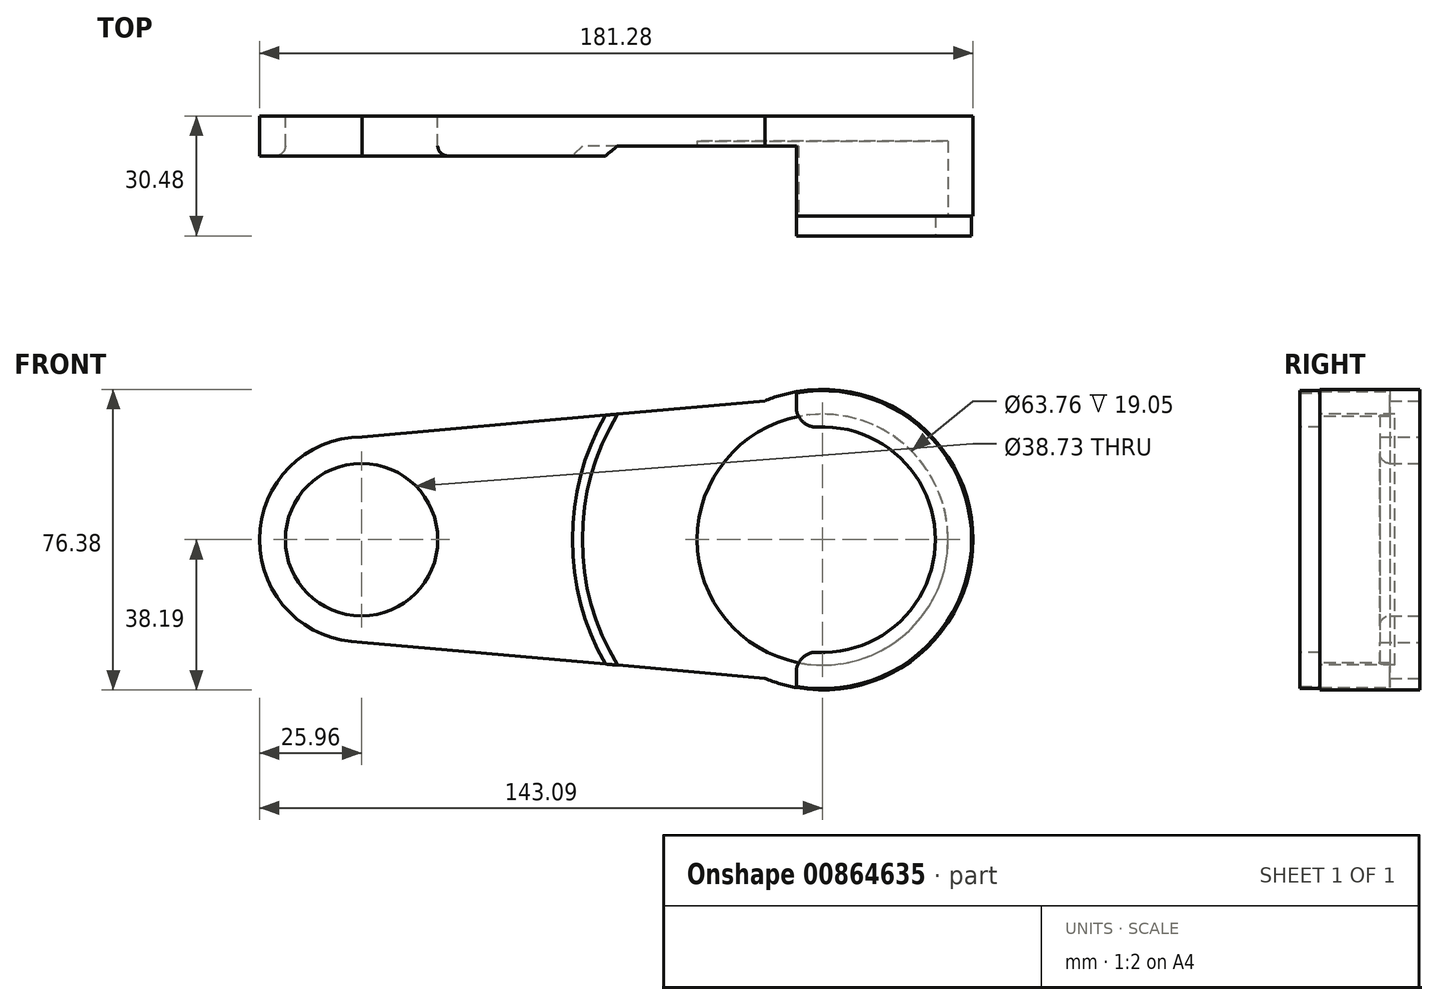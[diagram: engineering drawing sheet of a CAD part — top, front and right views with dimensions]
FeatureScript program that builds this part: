
annotation { "Feature Type Name" : "Feature", "Feature Type Description" : "" }
export const myFeature = defineFeature(function(context is Context, id is Id, definition is map)
    precondition{}
    {
        {
            var Q0;
            Q0=qCreatedBy(makeId("Front.planeOp"),FACE);
            var sketch = newSketch(context, id + "F0", { "sketchPlane" : qUnion([Q0])});
            skCircle(sketch, "E0", {"center": v(0, 0) * mm, "radius": 38.2 * mm});
            skSolve(sketch);
        }
        {
            var Q0;
            Q0 = qSketchRegion(id + "F0", true);
            extrude(context, id + "F1", {"entities" : qUnion([Q0]), "depth" : 25.4 * mm, "offsetDistance" : 25.4 * mm});
        }
        {
            var Q0;
            Q0=makeQuery(id+"F1.opExtrude","CAP_FACE",FACE,{"disambiguationData":[OSD([sQuery(id+"F0.wireOp",EDGE,"E0")])],"isStart":false});
            var sketch = newSketch(context, id + "F2", { "sketchPlane" : qUnion([Q0])});
            skCircle(sketch, "E1", {"center": v(0, 0) * mm, "radius": 31.88 * mm});
            skSolve(sketch);
        }
        {
            var Q0;
            Q0=makeQuery(id+"F2.imprint","IMPRINT",FACE,{"disambiguationData":[TD([[makeQuery(id+"F2.imprint","IMPRINT",EDGE,{"derivedFrom":sQuery(id+"F2.wireOp",EDGE,"E1")}),1.0]])]});
            extrude(context, id + "F3", {"entities" : qUnion([Q0]), "operationType" : NewBodyOperationType.REMOVE, "oppositeDirection" : true, "depth" : 19.05 * mm, "offsetDistance" : 25.4 * mm});
        }
        {
            var Q0;
            Q0=makeQuery(id+"F1.opExtrude","CAP_FACE",FACE,{"disambiguationData":[OSD([sQuery(id+"F0.wireOp",EDGE,"E0")])],"isStart":false});
            var sketch = newSketch(context, id + "F4", { "sketchPlane" : qUnion([Q0])});
            skSolve(sketch);
        }
        {
            var Q0;
            Q0=makeQuery(id+"F4.imprint","IMPRINT",FACE,{"disambiguationData":[TD([[makeQuery(id+"F4.imprint","IMPRINT",EDGE,{"derivedFrom":makeQuery(id+"F1.opExtrude","CAP_EDGE",EDGE,{"disambiguationData":[OSD([sQuery(id+"F0.wireOp",EDGE,"E0")])],"isStart":false})}),1.0]])]});
            var sketch = newSketch(context, id + "F5", { "sketchPlane" : qUnion([Q0])});
            skCircle(sketch, "E2", {"center": v(0, 0) * mm, "radius": 37.85 * mm});
            skSolve(sketch);
        }
        {
            var Q0;
            Q0 = qSketchRegion(id + "F5", true);
            extrude(context, id + "F6", {"entities" : qUnion([Q0]), "operationType" : NewBodyOperationType.ADD, "depth" : 5.08 * mm, "offsetDistance" : 25.4 * mm});
        }
        {
            var Q0;
            Q0=makeQuery(id+"F6.opExtrude","CAP_FACE",FACE,{"disambiguationData":[OSD([sQuery(id+"F5.wireOp",EDGE,"E2")])],"isStart":false});
            var sketch = newSketch(context, id + "F7", { "sketchPlane" : qUnion([Q0])});
            skCircle(sketch, "E3", {"center": v(0, 0) * mm, "radius": 28.64 * mm});
            skSolve(sketch);
        }
        {
            var Q0;
            Q0 = qSketchRegion(id + "F7", true);
            extrude(context, id + "F8", {"entities" : qUnion([Q0]), "operationType" : NewBodyOperationType.REMOVE, "oppositeDirection" : true, "depth" : 12.7 * mm, "offsetDistance" : 25.4 * mm});
        }
        {
            var Q0;
            Q0=makeQuery(id+"F6.opExtrude","CAP_FACE",FACE,{"disambiguationData":[OSD([sQuery(id+"F5.wireOp",EDGE,"E2")])],"isStart":false});
            var sketch = newSketch(context, id + "F9", { "sketchPlane" : qUnion([Q0])});
            skLineSegment(sketch, "E4.bottom", {"start": v(-6.69, -40.15) * mm, "end": v(-39.86, -40.15) * mm});
            skLineSegment(sketch, "E4.top", {"start": v(-6.69, 48.78) * mm, "end": v(-39.86, 48.78) * mm});
            skLineSegment(sketch, "E4.left", {"start": v(-6.69, -40.15) * mm, "end": v(-6.69, 48.78) * mm});
            skLineSegment(sketch, "E4.right", {"start": v(-39.86, -40.15) * mm, "end": v(-39.86, 48.78) * mm});
            skSolve(sketch);
        }
        {
            var Q0;
            Q0 = qSketchRegion(id + "F9", true);
            extrude(context, id + "F10", {"entities" : qUnion([Q0]), "operationType" : NewBodyOperationType.REMOVE, "oppositeDirection" : true, "depth" : 22.86 * mm, "offsetDistance" : 25.4 * mm});
        }
        {
            var Q0;
            Q0=makeQuery(id+"F10.boolean.opBoolean","INTERSECT",EDGE,{"disambiguationData":[OD(1.0)],"derivedFrom":[makeQuery(id+"F8.boolean.opBoolean","COPY",FACE,{"derivedFrom":makeQuery(id+"F8.opExtrude","SWEPT_FACE",FACE,{"disambiguationData":[OSD([sQuery(id+"F7.wireOp",EDGE,"E3")])]})}),makeQuery(id+"F10.opExtrude","SWEPT_FACE",FACE,{"disambiguationData":[OSD([sQuery(id+"F9.wireOp",EDGE,"E4.left")])]})]});
            var Q1;
            Q1=makeQuery(id+"F10.boolean.opBoolean","INTERSECT",EDGE,{"disambiguationData":[OD(0.0)],"derivedFrom":[makeQuery(id+"F8.boolean.opBoolean","COPY",FACE,{"derivedFrom":makeQuery(id+"F8.opExtrude","SWEPT_FACE",FACE,{"disambiguationData":[OSD([sQuery(id+"F7.wireOp",EDGE,"E3")])]})}),makeQuery(id+"F10.opExtrude","SWEPT_FACE",FACE,{"disambiguationData":[OSD([sQuery(id+"F9.wireOp",EDGE,"E4.left")])]})]});
            fillet(context, id + "F11", {"entities" : qUnion([Q0, Q1]), "radius" : 5.08 * mm, "tangentPropagation" : true, "allowEdgeOverflow" : false});
        }
        {
            var Q0;
            Q0=makeQuery(id+"F0.imprint","IMPRINT",FACE,{"disambiguationData":[TD([[makeQuery(id+"F0.imprint","IMPRINT",EDGE,{"derivedFrom":sQuery(id+"F0.wireOp",EDGE,"E0")}),1.0]])]});
            var sketch = newSketch(context, id + "F12", { "sketchPlane" : qUnion([Q0])});
            skPoint(sketch, "E5.middle", {"position": v(0, 0) * mm});
            skCircle(sketch, "E6", {"center": v(-117.03, 0) * mm, "radius": 26.06 * mm});
            skLineSegment(sketch, "E7.bottom", {"start": v(0, 36.57) * mm, "end": v(0, 36.57) * mm});
            skLineSegment(sketch, "E7.top", {"start": v(0, -36.57) * mm, "end": v(0, -36.57) * mm});
            skLineSegment(sketch, "E7.left", {"start": v(0, 36.57) * mm, "end": v(0, -36.57) * mm});
            skLineSegment(sketch, "E7.right", {"start": v(0, 36.57) * mm, "end": v(0, -36.57) * mm});
            skLineSegment(sketch, "E8", {"start": v(0, 36.57) * mm, "end": v(-117.03, 26.06) * mm});
            skLineSegment(sketch, "E9", {"start": v(0, -36.57) * mm, "end": v(-117.03, -26.06) * mm});
            skSolve(sketch);
        }
        {
            var Q0;
            {var subQ0=sQuery(id+"F12.wireOp",EDGE,"E8");var subQ1=sQuery(id+"F12.wireOp",EDGE,"E6");var subQ2=makeQuery(id+"F12.imprint","INTERSECT",VERTEX,{"derivedFrom":[subQ1,subQ0]});Q0=makeQuery(id+"F12.imprint","IMPRINT",FACE,{"disambiguationData":[TD([[makeQuery(id+"F12.imprint","IMPRINT",EDGE,{"disambiguationData":[TD([[subQ2,1.0]])],"derivedFrom":subQ1}),-1.0]])]});}
            var Q1;
            {var subQ0=sQuery(id+"F12.wireOp",EDGE,"E6");var subQ1=makeQuery(id+"F12.imprint","INTERSECT",VERTEX,{"derivedFrom":[subQ0,sQuery(id+"F12.wireOp",EDGE,"E8")]});Q1=makeQuery(id+"F12.imprint","IMPRINT",FACE,{"disambiguationData":[TD([[makeQuery(id+"F12.imprint","IMPRINT",EDGE,{"disambiguationData":[TD([[subQ1,-1.0]])],"derivedFrom":subQ0}),1.0]])]});}
            extrude(context, id + "F13", {"entities" : qUnion([Q0, Q1]), "operationType" : NewBodyOperationType.ADD, "depth" : 10.16 * mm, "offsetDistance" : 25.4 * mm});
        }
        {
            var Q0;
            Q0=makeQuery(id+"F13.opExtrude","CAP_EDGE",EDGE,{"disambiguationData":[OSD([sQuery(id+"F0.wireOp",EDGE,"E0")])],"isStart":false});
            chamfer(context, id + "F14", {"entities" : qUnion([Q0]), "width" : 25.4 * mm, "tangentPropagation" : true});
        }
        {
            var Q0;
            {var subQ0=sQuery(id+"F12.wireOp",EDGE,"E6");var subQ1=makeQuery(id+"F12.imprint","INTERSECT",VERTEX,{"derivedFrom":[subQ0,sQuery(id+"F12.wireOp",EDGE,"E8")]});Q0=makeQuery(id+"F12.imprint","IMPRINT",FACE,{"disambiguationData":[TD([[makeQuery(id+"F12.imprint","IMPRINT",EDGE,{"disambiguationData":[TD([[subQ1,-1.0]])],"derivedFrom":subQ0}),1.0]])]});}
            var sketch = newSketch(context, id + "F15", { "sketchPlane" : qUnion([Q0])});
            skCircle(sketch, "E10", {"center": v(-117.13, 0) * mm, "radius": 19.36 * mm});
            skSolve(sketch);
        }
        {
            var Q0;
            Q0 = qSketchRegion(id + "F15", true);
            extrude(context, id + "F16", {"entities" : qUnion([Q0]), "operationType" : NewBodyOperationType.REMOVE, "depth" : 19.05 * mm, "offsetDistance" : 25.4 * mm});
        }
        {
            var Q0;
            Q0=makeQuery(id+"F16.boolean.opBoolean","INTERSECT",EDGE,{"derivedFrom":[makeQuery(id+"F13.opExtrude","CAP_FACE",FACE,{"disambiguationData":[OSD([sQuery(id+"F0.wireOp",EDGE,"E0"),sQuery(id+"F12.wireOp",EDGE,"E6"),sQuery(id+"F12.wireOp",EDGE,"E8"),sQuery(id+"F12.wireOp",EDGE,"E9")])],"isStart":false}),makeQuery(id+"F16.opExtrude","SWEPT_FACE",FACE,{"disambiguationData":[OSD([sQuery(id+"F15.wireOp",EDGE,"E10")])]})]});
            fillet(context, id + "F17", {"entities" : qUnion([Q0]), "radius" : 2.54 * mm, "tangentPropagation" : true, "allowEdgeOverflow" : false});
        }
    });
